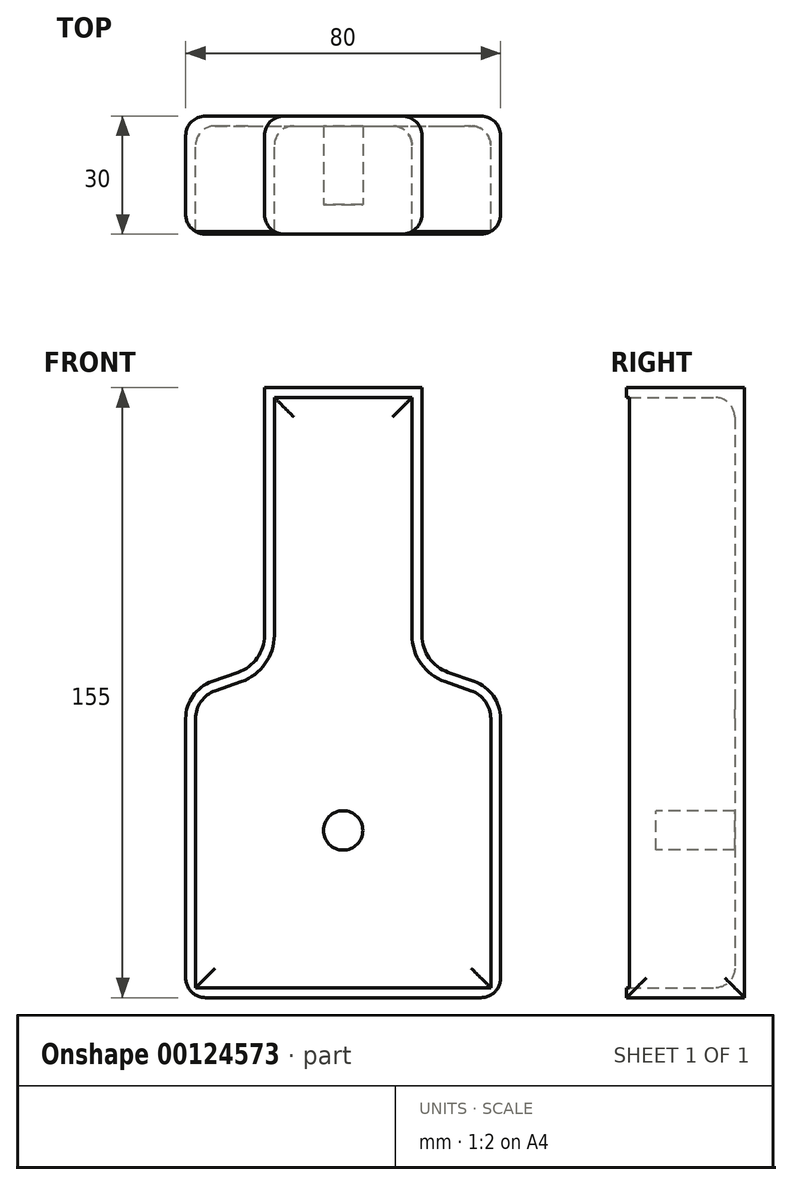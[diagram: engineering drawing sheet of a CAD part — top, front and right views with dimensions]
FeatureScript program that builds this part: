
annotation { "Feature Type Name" : "Feature", "Feature Type Description" : "" }
export const myFeature = defineFeature(function(context is Context, id is Id, definition is map)
    precondition{}
    {
        {
            var Q0;
            Q0=qCreatedBy(makeId("Front.planeOp"),FACE);
            var sketch = newSketch(context, id + "F0", { "sketchPlane" : qUnion([Q0])});
            skLineSegment(sketch, "E0", {"start": v(0, 0) * mm, "end": v(20, 0) * mm});
            skLineSegment(sketch, "E1", {"start": v(20, 0) * mm, "end": v(20, -62.92) * mm});
            skLineSegment(sketch, "E2", {"start": v(26.68, -72.35) * mm, "end": v(33.32, -74.68) * mm});
            skLineSegment(sketch, "E3", {"start": v(40, -84.12) * mm, "end": v(40, -155) * mm});
            skLineSegment(sketch, "E4", {"start": v(0, 53.96) * mm, "end": v(0, -80.6) * mm, "construction": true});
            skLineSegment(sketch, "E5", {"start": v(40, -155) * mm, "end": v(0, -155) * mm});
            skLineSegment(sketch, "E6.MirrorCS", {"start": v(-20, 0) * mm, "end": v(-20, -62.92) * mm});
            skLineSegment(sketch, "E7.MirrorCS", {"start": v(-26.68, -72.35) * mm, "end": v(-33.32, -74.68) * mm});
            skLineSegment(sketch, "E8.MirrorCS", {"start": v(-40, -84.12) * mm, "end": v(-40, -155) * mm});
            skLineSegment(sketch, "E9.MirrorCS", {"start": v(-40, -155) * mm, "end": v(0, -155) * mm});
            skLineSegment(sketch, "E10.MirrorCS", {"start": v(0, 0) * mm, "end": v(-20, 0) * mm});
            skPoint(sketch, "E11.visualSharp", {"position": v(-20, -70) * mm});
            skArc(sketch, "E11.filletArc", {"start": v(-26.68, -72.35) * mm, "mid": v(-21.84, -68.7) * mm, "end": v(-20, -62.92) * mm});
            skPoint(sketch, "E12.visualSharp", {"position": v(20, -70) * mm});
            skArc(sketch, "E12.filletArc", {"start": v(20, -62.92) * mm, "mid": v(21.84, -68.7) * mm, "end": v(26.68, -72.35) * mm});
            skPoint(sketch, "E13.visualSharp", {"position": v(-40, -77.03) * mm});
            skArc(sketch, "E13.filletArc", {"start": v(-33.32, -74.68) * mm, "mid": v(-38.16, -78.34) * mm, "end": v(-40, -84.12) * mm});
            skPoint(sketch, "E14.visualSharp", {"position": v(40, -77.03) * mm});
            skArc(sketch, "E14.filletArc", {"start": v(40, -84.12) * mm, "mid": v(38.16, -78.34) * mm, "end": v(33.32, -74.68) * mm});
            skSolve(sketch);
        }
        {
            var Q0;
            Q0=makeQuery(id+"F0.imprint","IMPRINT",FACE,{"disambiguationData":[TD([[makeQuery(id+"F0.imprint","IMPRINT",EDGE,{"derivedFrom":sQuery(id+"F0.wireOp",EDGE,"E0")}),-1.0]])]});
            extrude(context, id + "F1", {"entities" : qUnion([Q0]), "depth" : 30 * mm});
        }
        {
            var Q0;
            Q0=makeQuery(id+"F1.opExtrude","CAP_FACE",FACE,{"disambiguationData":[OSD([sQuery(id+"F0.wireOp",EDGE,"E0"),sQuery(id+"F0.wireOp",EDGE,"E1"),sQuery(id+"F0.wireOp",EDGE,"E2"),sQuery(id+"F0.wireOp",EDGE,"E3"),sQuery(id+"F0.wireOp",EDGE,"E5"),sQuery(id+"F0.wireOp",EDGE,"E6.MirrorCS"),sQuery(id+"F0.wireOp",EDGE,"E7.MirrorCS"),sQuery(id+"F0.wireOp",EDGE,"E8.MirrorCS"),sQuery(id+"F0.wireOp",EDGE,"E9.MirrorCS"),sQuery(id+"F0.wireOp",EDGE,"E10.MirrorCS")])],"isStart":false});
            shell(context, id + "F2", {"entities" : qUnion([Q0]), "thickness" : 2.5 * mm});
        }
        {
            var Q0;
            Q0=makeQuery(id+"F1.opExtrude","SWEPT_FACE",FACE,{"disambiguationData":[OSD([sQuery(id+"F0.wireOp",EDGE,"E8.MirrorCS")])]});
            var Q1;
            Q1=makeQuery(id+"F1.opExtrude","SWEPT_FACE",FACE,{"disambiguationData":[OSD([sQuery(id+"F0.wireOp",EDGE,"E3")])]});
            fillet(context, id + "F3", {"entities" : qUnion([Q0, Q1]), "radius" : 5 * mm, "tangentPropagation" : true, "allowEdgeOverflow" : false});
        }
        {
            var Q0;
            Q0=makeQuery(id+"F2.opShell","OFFSET_FACE",FACE,{"disambiguationData":[OSD([sQuery(id+"F0.wireOp",EDGE,"E0"),sQuery(id+"F0.wireOp",EDGE,"E1"),sQuery(id+"F0.wireOp",EDGE,"E2"),sQuery(id+"F0.wireOp",EDGE,"E3"),sQuery(id+"F0.wireOp",EDGE,"E5"),sQuery(id+"F0.wireOp",EDGE,"E6.MirrorCS"),sQuery(id+"F0.wireOp",EDGE,"E7.MirrorCS"),sQuery(id+"F0.wireOp",EDGE,"E8.MirrorCS"),sQuery(id+"F0.wireOp",EDGE,"E9.MirrorCS"),sQuery(id+"F0.wireOp",EDGE,"E10.MirrorCS"),sQuery(id+"F0.wireOp",EDGE,"E11.filletArc"),sQuery(id+"F0.wireOp",EDGE,"E12.filletArc"),sQuery(id+"F0.wireOp",EDGE,"E13.filletArc"),sQuery(id+"F0.wireOp",EDGE,"E14.filletArc")])]});
            cPlane(context, id + "F4", {"entities" : qUnion([Q0]), "cplaneType" : CPlaneType.OFFSET, "offset" : 20 * mm, "width" : 150 * mm, "height" : 150 * mm});
        }
        {
            var Q0;
            Q0=qCreatedBy(id+"F4.planeOp",FACE);
            var sketch = newSketch(context, id + "F5", { "sketchPlane" : qUnion([Q0])});
            skCircle(sketch, "E15", {"center": v(0, -112.5) * mm, "radius": 5 * mm});
            skLineSegment(sketch, "E16.0", {"start": v(-15, -2.5) * mm, "end": v(15, -2.5) * mm});
            skSolve(sketch);
        }
        {
            var Q0;
            Q0=makeQuery(id+"F5.imprint","IMPRINT",FACE,{"disambiguationData":[TD([[makeQuery(id+"F5.imprint","IMPRINT",EDGE,{"derivedFrom":sQuery(id+"F5.wireOp",EDGE,"E15")}),1.0]])]});
            extrude(context, id + "F6", {"entities" : qUnion([Q0]), "operationType" : NewBodyOperationType.ADD, "oppositeDirection" : true, "depth" : 20 * mm});
        }
        {
            var Q0;
            {var subQ0=sQuery(id+"F0.wireOp",EDGE,"E8.MirrorCS");Q0=makeQuery(id+"F2.opShell","OFFSET_EDGE",EDGE,{"disambiguationData":[OSD([subQ0]),TDD([makeQuery(id+"F1.opExtrude","CAP_EDGE",EDGE,{"disambiguationData":[OSD([subQ0])],"isStart":true})])]});}
            var Q1;
            {var subQ0=sQuery(id+"F0.wireOp",EDGE,"E9.MirrorCS");var subQ1=sQuery(id+"F0.wireOp",EDGE,"E5");Q1=makeQuery(id+"F2.opShell","OFFSET_EDGE",EDGE,{"disambiguationData":[OSD([subQ1,subQ0]),TDD([makeQuery(id+"F1.opExtrude","CAP_EDGE",EDGE,{"disambiguationData":[OSD([subQ1,subQ0])],"isStart":true})])]});}
            var Q2;
            {var subQ0=sQuery(id+"F0.wireOp",EDGE,"E10.MirrorCS");var subQ1=sQuery(id+"F0.wireOp",EDGE,"E0");Q2=makeQuery(id+"F2.opShell","OFFSET_EDGE",EDGE,{"disambiguationData":[OSD([subQ1,subQ0]),TDD([makeQuery(id+"F1.opExtrude","CAP_EDGE",EDGE,{"disambiguationData":[OSD([subQ1,subQ0])],"isStart":true})])]});}
            var Q3;
            {var subQ0=sQuery(id+"F0.wireOp",EDGE,"E1");Q3=makeQuery(id+"F2.opShell","OFFSET_EDGE",EDGE,{"disambiguationData":[OSD([subQ0]),TDD([makeQuery(id+"F1.opExtrude","CAP_EDGE",EDGE,{"disambiguationData":[OSD([subQ0])],"isStart":true})])]});}
            fillet(context, id + "F7", {"entities" : qUnion([Q0, Q1, Q2, Q3]), "radius" : 5 * mm, "tangentPropagation" : true, "allowEdgeOverflow" : false});
        }
    });
